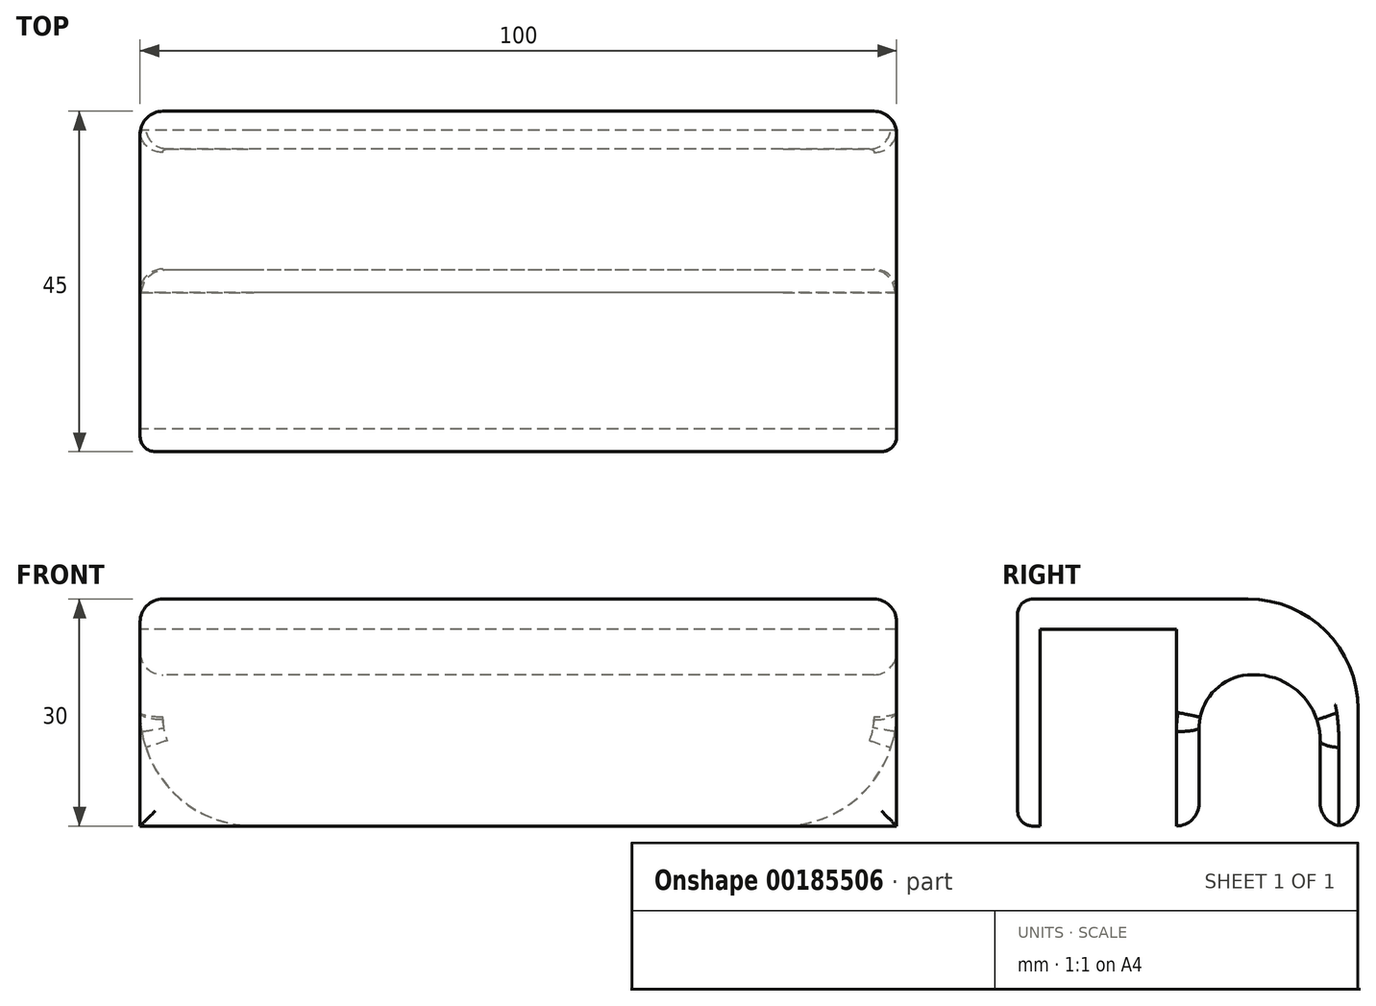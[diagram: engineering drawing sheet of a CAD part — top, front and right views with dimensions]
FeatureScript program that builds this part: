
annotation { "Feature Type Name" : "Feature", "Feature Type Description" : "" }
export const myFeature = defineFeature(function(context is Context, id is Id, definition is map)
    precondition{}
    {
        {
            var Q0;
            Q0=qCreatedBy(makeId("Right.planeOp"),FACE);
            var sketch = newSketch(context, id + "F0", { "sketchPlane" : qUnion([Q0])});
            skLineSegment(sketch, "E0", {"start": v(0, 0) * mm, "end": v(0, 30) * mm});
            skLineSegment(sketch, "E1", {"start": v(0, 30) * mm, "end": v(30.47, 30) * mm});
            skLineSegment(sketch, "E2", {"start": v(45, 15.47) * mm, "end": v(45, 0) * mm});
            skLineSegment(sketch, "E3", {"start": v(45, 0) * mm, "end": v(40, 0) * mm});
            skLineSegment(sketch, "E4", {"start": v(40, 0) * mm, "end": v(40, 11.3) * mm});
            skLineSegment(sketch, "E5", {"start": v(31.3, 20) * mm, "end": v(31.02, 20) * mm});
            skLineSegment(sketch, "E6", {"start": v(24, 12.98) * mm, "end": v(24, 0) * mm});
            skLineSegment(sketch, "E7", {"start": v(24, 0) * mm, "end": v(21, 0) * mm});
            skLineSegment(sketch, "E8", {"start": v(21, 0) * mm, "end": v(21, 26) * mm});
            skLineSegment(sketch, "E9", {"start": v(21, 26) * mm, "end": v(3, 26) * mm});
            skLineSegment(sketch, "E10", {"start": v(3, 26) * mm, "end": v(3, 0) * mm});
            skLineSegment(sketch, "E11", {"start": v(3, 0) * mm, "end": v(0, 0) * mm});
            skPoint(sketch, "E12.visualSharp", {"position": v(45, 30) * mm});
            skArc(sketch, "E12.filletArc", {"start": v(45, 15.47) * mm, "mid": v(40.74, 25.74) * mm, "end": v(30.47, 30) * mm});
            skPoint(sketch, "E13.visualSharp", {"position": v(40, 20) * mm});
            skArc(sketch, "E13.filletArc", {"start": v(40, 11.3) * mm, "mid": v(37.45, 17.45) * mm, "end": v(31.3, 20) * mm});
            skPoint(sketch, "E14.visualSharp", {"position": v(24, 20) * mm});
            skArc(sketch, "E14.filletArc", {"start": v(31.02, 20) * mm, "mid": v(26.06, 17.94) * mm, "end": v(24, 12.98) * mm});
            skSolve(sketch);
        }
        {
            var Q0;
            Q0 = qSketchRegion(id + "F0", true);
            extrude(context, id + "F1", {"entities" : qUnion([Q0]), "depth" : 100 * mm});
        }
        {
            var Q0;
            Q0=makeQuery(id+"F1.opExtrude","CAP_EDGE",EDGE,{"disambiguationData":[OSD([sQuery(id+"F0.wireOp",EDGE,"E7")])],"isStart":false});
            var Q1;
            Q1=makeQuery(id+"F1.opExtrude","CAP_EDGE",EDGE,{"disambiguationData":[OSD([sQuery(id+"F0.wireOp",EDGE,"E3")])],"isStart":false});
            var Q2;
            Q2=makeQuery(id+"F1.opExtrude","CAP_EDGE",EDGE,{"disambiguationData":[OSD([sQuery(id+"F0.wireOp",EDGE,"E7")])],"isStart":true});
            var Q3;
            Q3=makeQuery(id+"F1.opExtrude","CAP_EDGE",EDGE,{"disambiguationData":[OSD([sQuery(id+"F0.wireOp",EDGE,"E3")])],"isStart":true});
            fillet(context, id + "F2", {"entities" : qUnion([Q0, Q1, Q2, Q3]), "radius" : 15 * mm, "tangentPropagation" : true, "allowEdgeOverflow" : false});
        }
        {
            var Q0;
            Q0=makeQuery(id+"F1.opExtrude","SWEPT_EDGE",EDGE,{"disambiguationData":[OSD([sQuery(id+"F0.wireOp",EDGE,"E3"),sQuery(id+"F0.wireOp",EDGE,"E4")])]});
            var Q1;
            Q1=makeQuery(id+"F1.opExtrude","SWEPT_EDGE",EDGE,{"disambiguationData":[OSD([sQuery(id+"F0.wireOp",EDGE,"E2"),sQuery(id+"F0.wireOp",EDGE,"E3")])]});
            fillet(context, id + "F3", {"entities" : qUnion([Q0, Q1]), "radius" : 3 * mm, "tangentPropagation" : true, "allowEdgeOverflow" : false});
        }
        {
            var Q0;
            Q0=makeQuery(id+"F1.opExtrude","SWEPT_EDGE",EDGE,{"disambiguationData":[OSD([sQuery(id+"F0.wireOp",EDGE,"E0"),sQuery(id+"F0.wireOp",EDGE,"E1")])]});
            var Q1;
            Q1=makeQuery(id+"F1.opExtrude","SWEPT_EDGE",EDGE,{"disambiguationData":[OSD([sQuery(id+"F0.wireOp",EDGE,"E0"),sQuery(id+"F0.wireOp",EDGE,"E11")])]});
            fillet(context, id + "F4", {"entities" : qUnion([Q0, Q1]), "radius" : 2 * mm, "tangentPropagation" : true, "allowEdgeOverflow" : false});
        }
    });
